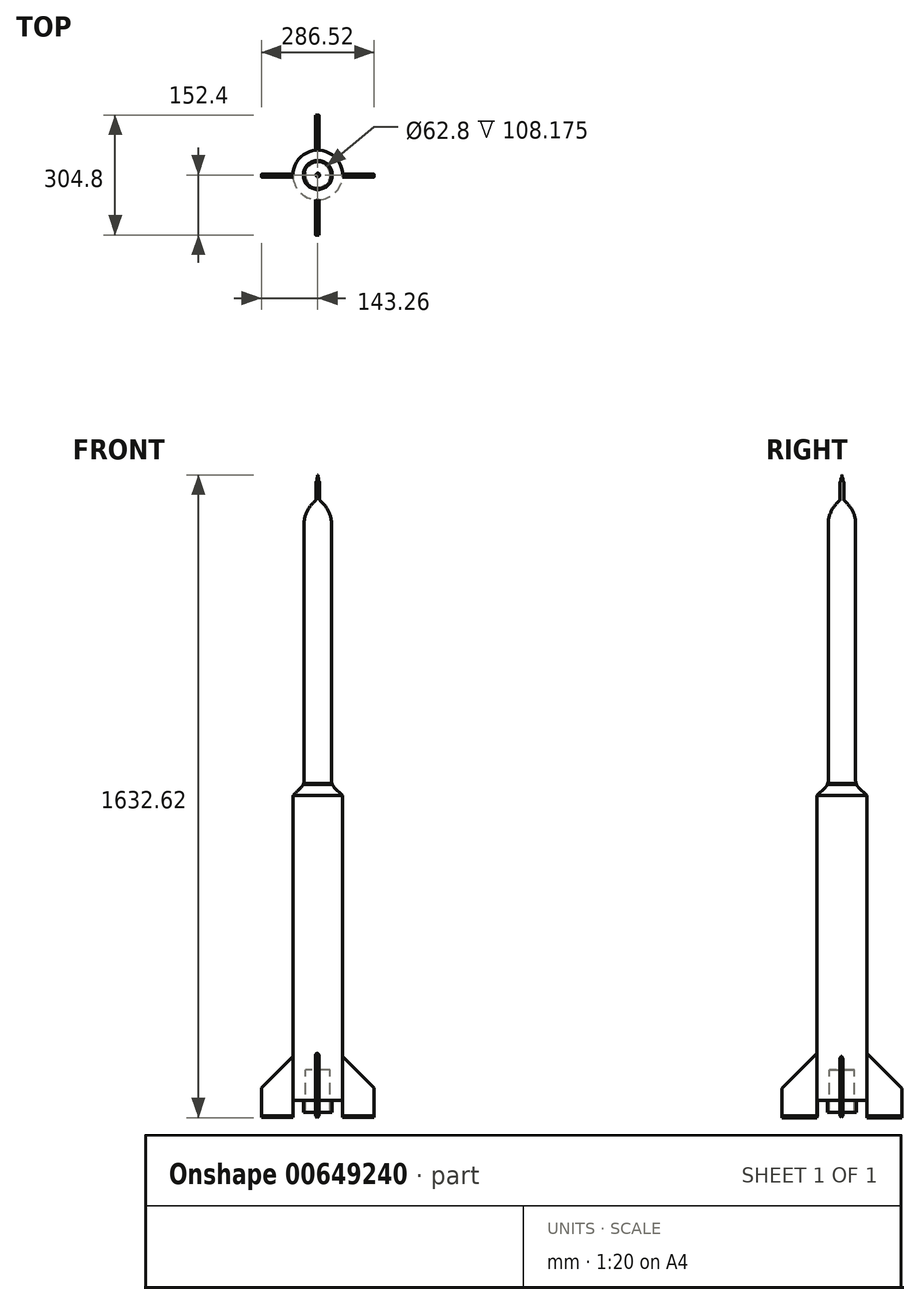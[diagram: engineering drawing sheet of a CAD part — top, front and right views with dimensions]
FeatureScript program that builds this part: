
annotation { "Feature Type Name" : "Feature", "Feature Type Description" : "" }
export const myFeature = defineFeature(function(context is Context, id is Id, definition is map)
    precondition{}
    {
        {
            var Q0;
            Q0=qCreatedBy(makeId("Top.planeOp"),FACE);
            var sketch = newSketch(context, id + "F0", { "sketchPlane" : qUnion([Q0])});
            skCircle(sketch, "E0", {"center": v(0, 0) * mm, "radius": 4.63 * mm});
            skSolve(sketch);
        }
        {
            var Q0;
            Q0 = qSketchRegion(id + "F0", true);
            extrude(context, id + "F1", {"entities" : qUnion([Q0]), "endBound" : BoundingType.SYMMETRIC, "depth" : 1539.24 * mm, "offsetDistance" : 25.4 * mm});
        }
        {
            var Q0;
            Q0=makeQuery(id+"F1.opExtrude","CAP_EDGE",EDGE,{"disambiguationData":[OSD([sQuery(id+"F0.wireOp",EDGE,"E0")])],"isStart":false});
            chamfer(context, id + "F2", {"entities" : qUnion([Q0]), "width" : 2.54 * mm, "tangentPropagation" : true});
        }
        {
            var Q0;
            Q0=qCreatedBy(makeId("Top.planeOp"),FACE);
            var sketch = newSketch(context, id + "F3", { "sketchPlane" : qUnion([Q0])});
            skCircle(sketch, "E1", {"center": v(0, 0) * mm, "radius": 2.08 * mm});
            skSolve(sketch);
        }
        {
            var Q0;
            Q0 = qSketchRegion(id + "F3", true);
            extrude(context, id + "F4", {"entities" : qUnion([Q0]), "operationType" : NewBodyOperationType.ADD, "depth" : 779.02 * mm, "offsetDistance" : 25.4 * mm});
        }
        {
            var Q0;
            Q0=makeQuery(id+"F4.opExtrude","CAP_EDGE",EDGE,{"disambiguationData":[OSD([sQuery(id+"F3.wireOp",EDGE,"E1")])],"isStart":false});
            chamfer(context, id + "F5", {"entities" : qUnion([Q0]), "width" : 2.03 * mm, "tangentPropagation" : true});
        }
        {
            var Q0;
            Q0=qCreatedBy(makeId("Top.planeOp"),FACE);
            var sketch = newSketch(context, id + "F6", { "sketchPlane" : qUnion([Q0])});
            skCircle(sketch, "E2", {"center": v(0, 0) * mm, "radius": 34.77 * mm});
            skSolve(sketch);
        }
        {
            var Q0;
            Q0 = qSketchRegion(id + "F6", true);
            extrude(context, id + "F7", {"entities" : qUnion([Q0]), "operationType" : NewBodyOperationType.ADD, "depth" : 720.85 * mm, "offsetDistance" : 25.4 * mm});
        }
        {
            var Q0;
            Q0=makeQuery(id+"F7.opExtrude","CAP_EDGE",EDGE,{"disambiguationData":[OSD([sQuery(id+"F6.wireOp",EDGE,"E2")])],"isStart":false});
            chamfer(context, id + "F8", {"entities" : qUnion([Q0]), "width" : 30.48 * mm, "tangentPropagation" : true});
        }
        {
            var Q0;
            Q0=qCreatedBy(makeId("Top.planeOp"),FACE);
            var sketch = newSketch(context, id + "F9", { "sketchPlane" : qUnion([Q0])});
            skCircle(sketch, "E3", {"center": v(0, 0) * mm, "radius": 63.15 * mm});
            skSolve(sketch);
        }
        {
            var Q0;
            Q0 = qSketchRegion(id + "F9", true);
            extrude(context, id + "F10", {"entities" : qUnion([Q0]), "operationType" : NewBodyOperationType.ADD, "oppositeDirection" : true, "depth" : 774.7 * mm, "offsetDistance" : 25.4 * mm});
        }
        {
            var Q0;
            Q0=makeQuery(id+"F10.opExtrude","CAP_EDGE",EDGE,{"disambiguationData":[OSD([sQuery(id+"F9.wireOp",EDGE,"E3")])],"isStart":true});
            chamfer(context, id + "F11", {"entities" : qUnion([Q0]), "width" : 30.48 * mm, "tangentPropagation" : true});
        }
        {
            var Q0;
            Q0=makeQuery(id+"F11.opChamfer","BLEND_EDGE",EDGE,{"blendedFrom":[makeQuery(id+"F10.opExtrude","CAP_EDGE",EDGE,{"disambiguationData":[OSD([sQuery(id+"F9.wireOp",EDGE,"E3")])],"isStart":true}),makeQuery(id+"F7.opExtrude","SWEPT_FACE",FACE,{"disambiguationData":[OSD([sQuery(id+"F6.wireOp",EDGE,"E2")])]})],"blendedInto":[makeQuery(id+"F7.opExtrude","SWEPT_FACE",FACE,{"disambiguationData":[OSD([sQuery(id+"F6.wireOp",EDGE,"E2")])]})]});
            fillet(context, id + "F12", {"entities" : qUnion([Q0]), "radius" : 24.66 * mm, "tangentPropagation" : true, "allowEdgeOverflow" : false});
        }
        {
            var Q0;
            {var subQ0=sQuery(id+"F0.wireOp",EDGE,"E0");var subQ1=sQuery(id+"F6.wireOp",EDGE,"E2");Q0=makeQuery(id+"F8.opChamfer","BLEND_EDGE",EDGE,{"blendedFrom":[makeQuery(id+"F7.opExtrude","CAP_EDGE",EDGE,{"disambiguationData":[OSD([subQ1])],"isStart":false}),makeQuery(id+"F7.boolean.opBoolean","SPLIT",FACE,{"disambiguationData":[TD([makeQuery(id+"F2.opChamfer","BLEND_FACE",FACE,{"disambiguationData":[OSD([subQ0])]})])],"derivedFrom":makeQuery(id+"F1.opExtrude","SWEPT_FACE",FACE,{"disambiguationData":[OSD([subQ0])]})})],"blendedInto":[makeQuery(id+"F7.boolean.opBoolean","SPLIT",FACE,{"disambiguationData":[TD([makeQuery(id+"F2.opChamfer","BLEND_FACE",FACE,{"disambiguationData":[OSD([subQ0])]})])],"derivedFrom":makeQuery(id+"F1.opExtrude","SWEPT_FACE",FACE,{"disambiguationData":[OSD([subQ0])]})})]});}
            fillet(context, id + "F13", {"entities" : qUnion([Q0]), "radius" : 5.08 * mm, "tangentPropagation" : true, "allowEdgeOverflow" : false});
        }
        {
            var Q0;
            {var subQ0=sQuery(id+"F0.wireOp",EDGE,"E0");Q0=makeQuery(id+"F2.opChamfer","BLEND_EDGE",EDGE,{"blendedFrom":[makeQuery(id+"F1.opExtrude","CAP_EDGE",EDGE,{"disambiguationData":[OSD([subQ0])],"isStart":false}),makeQuery(id+"F1.opExtrude","CAP_FACE",FACE,{"disambiguationData":[OSD([subQ0])],"isStart":false})],"blendedInto":[makeQuery(id+"F1.opExtrude","CAP_FACE",FACE,{"disambiguationData":[OSD([subQ0])],"isStart":false})]});}
            fillet(context, id + "F14", {"entities" : qUnion([Q0]), "radius" : 2.47 * mm, "tangentPropagation" : true, "allowEdgeOverflow" : false});
        }
        {
            var Q0;
            {var subQ0=sQuery(id+"F0.wireOp",EDGE,"E0");Q0=makeQuery(id+"F14.opFillet","BLEND_EDGE",EDGE,{"blendedFrom":[makeQuery(id+"F2.opChamfer","BLEND_EDGE",EDGE,{"blendedFrom":[makeQuery(id+"F1.opExtrude","CAP_EDGE",EDGE,{"disambiguationData":[OSD([subQ0])],"isStart":false}),makeQuery(id+"F1.opExtrude","CAP_FACE",FACE,{"disambiguationData":[OSD([subQ0])],"isStart":false})],"blendedInto":[makeQuery(id+"F1.opExtrude","CAP_FACE",FACE,{"disambiguationData":[OSD([subQ0])],"isStart":false})]}),makeQuery(id+"F4.opExtrude","SWEPT_FACE",FACE,{"disambiguationData":[OSD([sQuery(id+"F3.wireOp",EDGE,"E1")])]})],"blendedInto":[makeQuery(id+"F4.opExtrude","SWEPT_FACE",FACE,{"disambiguationData":[OSD([sQuery(id+"F3.wireOp",EDGE,"E1")])]})]});}
            fillet(context, id + "F15", {"entities" : qUnion([Q0]), "radius" : 2.64 * mm, "tangentPropagation" : true, "allowEdgeOverflow" : false});
        }
        {
            var Q0;
            Q0=qCreatedBy(makeId("Front.planeOp"),FACE);
            var sketch = newSketch(context, id + "F16", { "sketchPlane" : qUnion([Q0])});
            skLineSegment(sketch, "E4.bottom", {"start": v(-6.05, -685.08) * mm, "end": v(2.72, -685.08) * mm});
            skLineSegment(sketch, "E4.top", {"start": v(-6.05, -803.66) * mm, "end": v(2.72, -803.66) * mm});
            skLineSegment(sketch, "E4.left", {"start": v(-6.05, -685.08) * mm, "end": v(-6.05, -803.66) * mm});
            skLineSegment(sketch, "E4.right", {"start": v(2.72, -685.08) * mm, "end": v(2.72, -803.66) * mm});
            skSolve(sketch);
        }
        {
            var Q0;
            Q0 = qSketchRegion(id + "F16", true);
            extrude(context, id + "F17", {"entities" : qUnion([Q0]), "operationType" : NewBodyOperationType.ADD, "endBound" : BoundingType.SYMMETRIC, "depth" : 304.8 * mm, "offsetDistance" : 25.4 * mm});
        }
        {
            var Q0;
            Q0=makeQuery(id+"F17.opExtrude","CAP_EDGE",EDGE,{"disambiguationData":[OSD([sQuery(id+"F16.wireOp",EDGE,"E4.bottom")])],"isStart":false});
            var Q1;
            Q1=makeQuery(id+"F17.opExtrude","CAP_EDGE",EDGE,{"disambiguationData":[OSD([sQuery(id+"F16.wireOp",EDGE,"E4.bottom")])],"isStart":true});
            chamfer(context, id + "F18", {"entities" : qUnion([Q0, Q1]), "width" : 88.9 * mm, "tangentPropagation" : true});
        }
        {
            var Q0;
            Q0=qCreatedBy(makeId("Right.planeOp"),FACE);
            var sketch = newSketch(context, id + "F19", { "sketchPlane" : qUnion([Q0])});
            skLineSegment(sketch, "E5.bottom", {"start": v(2.04, -683.97) * mm, "end": v(-4.75, -683.97) * mm});
            skLineSegment(sketch, "E5.top", {"start": v(2.04, -803.67) * mm, "end": v(-4.75, -803.67) * mm});
            skLineSegment(sketch, "E5.left", {"start": v(2.04, -683.97) * mm, "end": v(2.04, -803.67) * mm});
            skLineSegment(sketch, "E5.right", {"start": v(-4.75, -683.97) * mm, "end": v(-4.75, -803.67) * mm});
            skSolve(sketch);
        }
        {
            var Q0;
            Q0 = qSketchRegion(id + "F19", true);
            extrude(context, id + "F20", {"entities" : qUnion([Q0]), "operationType" : NewBodyOperationType.ADD, "endBound" : BoundingType.SYMMETRIC, "oppositeDirection" : true, "depth" : 286.5 * mm, "offsetDistance" : 25.4 * mm});
        }
        {
            var Q0;
            Q0=makeQuery(id+"F20.opExtrude","CAP_EDGE",EDGE,{"disambiguationData":[OSD([sQuery(id+"F19.wireOp",EDGE,"E5.bottom")])],"isStart":false});
            var Q1;
            Q1=makeQuery(id+"F20.opExtrude","CAP_EDGE",EDGE,{"disambiguationData":[OSD([sQuery(id+"F19.wireOp",EDGE,"E5.bottom")])],"isStart":true});
            chamfer(context, id + "F21", {"entities" : qUnion([Q0, Q1]), "width" : 88.9 * mm, "tangentPropagation" : true});
        }
        {
            var Q0;
            Q0=qCreatedBy(makeId("Top.planeOp"),FACE);
            var sketch = newSketch(context, id + "F22", { "sketchPlane" : qUnion([Q0])});
            skCircle(sketch, "E6", {"center": v(0, 0) * mm, "radius": 63.15 * mm});
            skSolve(sketch);
        }
        {
            var Q0;
            Q0 = qSketchRegion(id + "F22", true);
            extrude(context, id + "F23", {"entities" : qUnion([Q0]), "operationType" : NewBodyOperationType.ADD, "oppositeDirection" : true, "depth" : 805.18 * mm, "offsetDistance" : 25.4 * mm});
        }
        {
            var Q0;
            {var subQ0=sQuery(id+"F19.wireOp",EDGE,"E5.right");var subQ1=sQuery(id+"F19.wireOp",EDGE,"E5.left");var subQ2=sQuery(id+"F19.wireOp",EDGE,"E5.top");Q0=makeQuery(id+"F23.boolean.opBoolean","SPLIT",FACE,{"disambiguationData":[TD([makeQuery(id+"F20.opExtrude","CAP_FACE",FACE,{"disambiguationData":[OSD([sQuery(id+"F19.wireOp",EDGE,"E5.bottom"),subQ2,subQ1,subQ0])],"isStart":true})])],"derivedFrom":makeQuery(id+"F20.opExtrude","SWEPT_FACE",FACE,{"disambiguationData":[OSD([subQ2])]})});}
            var Q1;
            {var subQ2=sQuery(id+"F16.wireOp",EDGE,"E4.top");Q1=makeQuery(id+"F20.boolean.opBoolean","SPLIT",FACE,{"disambiguationData":[TD([makeQuery(id+"F20.opExtrude","SWEPT_FACE",FACE,{"disambiguationData":[OSD([sQuery(id+"F19.wireOp",EDGE,"E5.right")])]})])],"derivedFrom":makeQuery(id+"F17.opExtrude","SWEPT_FACE",FACE,{"disambiguationData":[OSD([subQ2])]})});}
            var Q2;
            {var subQ2=sQuery(id+"F16.wireOp",EDGE,"E4.top");Q2=makeQuery(id+"F20.boolean.opBoolean","SPLIT",FACE,{"disambiguationData":[TD([makeQuery(id+"F20.opExtrude","SWEPT_FACE",FACE,{"disambiguationData":[OSD([sQuery(id+"F19.wireOp",EDGE,"E5.left")])]})])],"derivedFrom":makeQuery(id+"F17.opExtrude","SWEPT_FACE",FACE,{"disambiguationData":[OSD([subQ2])]})});}
            var Q3;
            {var subQ0=sQuery(id+"F19.wireOp",EDGE,"E5.right");var subQ1=sQuery(id+"F19.wireOp",EDGE,"E5.left");var subQ2=sQuery(id+"F19.wireOp",EDGE,"E5.top");Q3=makeQuery(id+"F23.boolean.opBoolean","SPLIT",FACE,{"disambiguationData":[TD([makeQuery(id+"F20.opExtrude","CAP_FACE",FACE,{"disambiguationData":[OSD([sQuery(id+"F19.wireOp",EDGE,"E5.bottom"),subQ2,subQ1,subQ0])],"isStart":false})])],"derivedFrom":makeQuery(id+"F20.opExtrude","SWEPT_FACE",FACE,{"disambiguationData":[OSD([subQ2])]})});}
            extrude(context, id + "F24", {"entities" : qUnion([Q0, Q1, Q2, Q3]), "operationType" : NewBodyOperationType.ADD, "depth" : 45.72 * mm, "offsetDistance" : 25.4 * mm});
        }
        {
            var Q0;
            Q0=makeQuery(id+"F23.opExtrude","CAP_EDGE",EDGE,{"disambiguationData":[OSD([sQuery(id+"F22.wireOp",EDGE,"E6")])],"isStart":true});
            chamfer(context, id + "F25", {"entities" : qUnion([Q0]), "width" : 30.48 * mm, "tangentPropagation" : true});
        }
        {
            var Q0;
            Q0=makeQuery(id+"F21.opChamfer","BLEND_EDGE",EDGE,{"blendedFrom":[makeQuery(id+"F20.opExtrude","CAP_EDGE",EDGE,{"disambiguationData":[OSD([sQuery(id+"F19.wireOp",EDGE,"E5.bottom")])],"isStart":true}),makeQuery(id+"F20.opExtrude","SWEPT_FACE",FACE,{"disambiguationData":[OSD([sQuery(id+"F19.wireOp",EDGE,"E5.left")])]})],"blendedInto":[makeQuery(id+"F20.opExtrude","SWEPT_FACE",FACE,{"disambiguationData":[OSD([sQuery(id+"F19.wireOp",EDGE,"E5.left")])]})]});
            var Q1;
            Q1=makeQuery(id+"F21.opChamfer","BLEND_EDGE",EDGE,{"blendedFrom":[makeQuery(id+"F20.opExtrude","CAP_EDGE",EDGE,{"disambiguationData":[OSD([sQuery(id+"F19.wireOp",EDGE,"E5.bottom")])],"isStart":true}),makeQuery(id+"F20.opExtrude","SWEPT_FACE",FACE,{"disambiguationData":[OSD([sQuery(id+"F19.wireOp",EDGE,"E5.right")])]})],"blendedInto":[makeQuery(id+"F20.opExtrude","SWEPT_FACE",FACE,{"disambiguationData":[OSD([sQuery(id+"F19.wireOp",EDGE,"E5.right")])]})]});
            var Q2;
            Q2=makeQuery(id+"F18.opChamfer","BLEND_EDGE",EDGE,{"blendedFrom":[makeQuery(id+"F17.opExtrude","CAP_EDGE",EDGE,{"disambiguationData":[OSD([sQuery(id+"F16.wireOp",EDGE,"E4.bottom")])],"isStart":true}),makeQuery(id+"F17.opExtrude","SWEPT_FACE",FACE,{"disambiguationData":[OSD([sQuery(id+"F16.wireOp",EDGE,"E4.right")])]})],"blendedInto":[makeQuery(id+"F17.opExtrude","SWEPT_FACE",FACE,{"disambiguationData":[OSD([sQuery(id+"F16.wireOp",EDGE,"E4.right")])]})]});
            var Q3;
            Q3=makeQuery(id+"F18.opChamfer","BLEND_EDGE",EDGE,{"blendedFrom":[makeQuery(id+"F17.opExtrude","CAP_EDGE",EDGE,{"disambiguationData":[OSD([sQuery(id+"F16.wireOp",EDGE,"E4.bottom")])],"isStart":true}),makeQuery(id+"F17.opExtrude","SWEPT_FACE",FACE,{"disambiguationData":[OSD([sQuery(id+"F16.wireOp",EDGE,"E4.left")])]})],"blendedInto":[makeQuery(id+"F17.opExtrude","SWEPT_FACE",FACE,{"disambiguationData":[OSD([sQuery(id+"F16.wireOp",EDGE,"E4.left")])]})]});
            var Q4;
            Q4=makeQuery(id+"F21.opChamfer","BLEND_EDGE",EDGE,{"blendedFrom":[makeQuery(id+"F20.opExtrude","CAP_EDGE",EDGE,{"disambiguationData":[OSD([sQuery(id+"F19.wireOp",EDGE,"E5.bottom")])],"isStart":false}),makeQuery(id+"F20.opExtrude","SWEPT_FACE",FACE,{"disambiguationData":[OSD([sQuery(id+"F19.wireOp",EDGE,"E5.left")])]})],"blendedInto":[makeQuery(id+"F20.opExtrude","SWEPT_FACE",FACE,{"disambiguationData":[OSD([sQuery(id+"F19.wireOp",EDGE,"E5.left")])]})]});
            var Q5;
            Q5=makeQuery(id+"F21.opChamfer","BLEND_EDGE",EDGE,{"blendedFrom":[makeQuery(id+"F20.opExtrude","CAP_EDGE",EDGE,{"disambiguationData":[OSD([sQuery(id+"F19.wireOp",EDGE,"E5.bottom")])],"isStart":false}),makeQuery(id+"F20.opExtrude","SWEPT_FACE",FACE,{"disambiguationData":[OSD([sQuery(id+"F19.wireOp",EDGE,"E5.right")])]})],"blendedInto":[makeQuery(id+"F20.opExtrude","SWEPT_FACE",FACE,{"disambiguationData":[OSD([sQuery(id+"F19.wireOp",EDGE,"E5.right")])]})]});
            var Q6;
            Q6=makeQuery(id+"F18.opChamfer","BLEND_EDGE",EDGE,{"blendedFrom":[makeQuery(id+"F17.opExtrude","CAP_EDGE",EDGE,{"disambiguationData":[OSD([sQuery(id+"F16.wireOp",EDGE,"E4.bottom")])],"isStart":false}),makeQuery(id+"F17.opExtrude","SWEPT_FACE",FACE,{"disambiguationData":[OSD([sQuery(id+"F16.wireOp",EDGE,"E4.right")])]})],"blendedInto":[makeQuery(id+"F17.opExtrude","SWEPT_FACE",FACE,{"disambiguationData":[OSD([sQuery(id+"F16.wireOp",EDGE,"E4.right")])]})]});
            var Q7;
            Q7=makeQuery(id+"F18.opChamfer","BLEND_EDGE",EDGE,{"blendedFrom":[makeQuery(id+"F17.opExtrude","CAP_EDGE",EDGE,{"disambiguationData":[OSD([sQuery(id+"F16.wireOp",EDGE,"E4.bottom")])],"isStart":false}),makeQuery(id+"F17.opExtrude","SWEPT_FACE",FACE,{"disambiguationData":[OSD([sQuery(id+"F16.wireOp",EDGE,"E4.left")])]})],"blendedInto":[makeQuery(id+"F17.opExtrude","SWEPT_FACE",FACE,{"disambiguationData":[OSD([sQuery(id+"F16.wireOp",EDGE,"E4.left")])]})]});
            fillet(context, id + "F26", {"entities" : qUnion([Q0, Q1, Q2, Q3, Q4, Q5, Q6, Q7]), "radius" : 5.08 * mm, "tangentPropagation" : true, "allowEdgeOverflow" : false});
        }
        {
            var Q0;
            {var subQ0=sQuery(id+"F16.wireOp",EDGE,"E4.left");var subQ1=sQuery(id+"F16.wireOp",EDGE,"E4.top");Q0=makeQuery(id+"F24.opExtrude","CAP_EDGE",EDGE,{"disambiguationData":[OSD([subQ1,subQ0]),TDD([makeQuery(id+"F20.boolean.opBoolean","SPLIT",EDGE,{"disambiguationData":[TD([makeQuery(id+"F20.opExtrude","SWEPT_FACE",FACE,{"disambiguationData":[OSD([sQuery(id+"F19.wireOp",EDGE,"E5.right")])]})])],"derivedFrom":makeQuery(id+"F17.opExtrude","SWEPT_EDGE",EDGE,{"disambiguationData":[OSD([subQ1,subQ0])]})})])],"isStart":false});}
            var Q1;
            {var subQ0=sQuery(id+"F16.wireOp",EDGE,"E4.right");var subQ1=sQuery(id+"F16.wireOp",EDGE,"E4.top");Q1=makeQuery(id+"F24.opExtrude","CAP_EDGE",EDGE,{"disambiguationData":[OSD([subQ1,subQ0]),TDD([makeQuery(id+"F20.boolean.opBoolean","SPLIT",EDGE,{"disambiguationData":[TD([makeQuery(id+"F20.opExtrude","SWEPT_FACE",FACE,{"disambiguationData":[OSD([sQuery(id+"F19.wireOp",EDGE,"E5.right")])]})])],"derivedFrom":makeQuery(id+"F17.opExtrude","SWEPT_EDGE",EDGE,{"disambiguationData":[OSD([subQ1,subQ0])]})})])],"isStart":false});}
            var Q2;
            {var subQ0=sQuery(id+"F19.wireOp",EDGE,"E5.left");var subQ1=sQuery(id+"F19.wireOp",EDGE,"E5.top");Q2=makeQuery(id+"F24.opExtrude","CAP_EDGE",EDGE,{"disambiguationData":[OSD([subQ1,subQ0]),TDD([makeQuery(id+"F23.boolean.opBoolean","SPLIT",EDGE,{"disambiguationData":[TD([makeQuery(id+"F20.opExtrude","CAP_FACE",FACE,{"disambiguationData":[OSD([sQuery(id+"F19.wireOp",EDGE,"E5.bottom"),subQ1,subQ0,sQuery(id+"F19.wireOp",EDGE,"E5.right")])],"isStart":false})])],"derivedFrom":makeQuery(id+"F20.opExtrude","SWEPT_EDGE",EDGE,{"disambiguationData":[OSD([subQ1,subQ0])]})})])],"isStart":false});}
            var Q3;
            {var subQ0=sQuery(id+"F19.wireOp",EDGE,"E5.right");var subQ1=sQuery(id+"F19.wireOp",EDGE,"E5.top");Q3=makeQuery(id+"F24.opExtrude","CAP_EDGE",EDGE,{"disambiguationData":[OSD([subQ1,subQ0]),TDD([makeQuery(id+"F23.boolean.opBoolean","SPLIT",EDGE,{"disambiguationData":[TD([makeQuery(id+"F20.opExtrude","CAP_FACE",FACE,{"disambiguationData":[OSD([sQuery(id+"F19.wireOp",EDGE,"E5.bottom"),subQ1,sQuery(id+"F19.wireOp",EDGE,"E5.left"),subQ0])],"isStart":false})])],"derivedFrom":makeQuery(id+"F20.opExtrude","SWEPT_EDGE",EDGE,{"disambiguationData":[OSD([subQ1,subQ0])]})})])],"isStart":false});}
            var Q4;
            {var subQ0=sQuery(id+"F16.wireOp",EDGE,"E4.left");var subQ1=sQuery(id+"F16.wireOp",EDGE,"E4.top");Q4=makeQuery(id+"F24.opExtrude","CAP_EDGE",EDGE,{"disambiguationData":[OSD([subQ1,subQ0]),TDD([makeQuery(id+"F20.boolean.opBoolean","SPLIT",EDGE,{"disambiguationData":[TD([makeQuery(id+"F20.opExtrude","SWEPT_FACE",FACE,{"disambiguationData":[OSD([sQuery(id+"F19.wireOp",EDGE,"E5.left")])]})])],"derivedFrom":makeQuery(id+"F17.opExtrude","SWEPT_EDGE",EDGE,{"disambiguationData":[OSD([subQ1,subQ0])]})})])],"isStart":false});}
            var Q5;
            {var subQ0=sQuery(id+"F16.wireOp",EDGE,"E4.right");var subQ1=sQuery(id+"F16.wireOp",EDGE,"E4.top");Q5=makeQuery(id+"F24.opExtrude","CAP_EDGE",EDGE,{"disambiguationData":[OSD([subQ1,subQ0]),TDD([makeQuery(id+"F20.boolean.opBoolean","SPLIT",EDGE,{"disambiguationData":[TD([makeQuery(id+"F20.opExtrude","SWEPT_FACE",FACE,{"disambiguationData":[OSD([sQuery(id+"F19.wireOp",EDGE,"E5.left")])]})])],"derivedFrom":makeQuery(id+"F17.opExtrude","SWEPT_EDGE",EDGE,{"disambiguationData":[OSD([subQ1,subQ0])]})})])],"isStart":false});}
            var Q6;
            {var subQ0=sQuery(id+"F19.wireOp",EDGE,"E5.right");var subQ1=sQuery(id+"F19.wireOp",EDGE,"E5.top");Q6=makeQuery(id+"F24.opExtrude","CAP_EDGE",EDGE,{"disambiguationData":[OSD([subQ1,subQ0]),TDD([makeQuery(id+"F23.boolean.opBoolean","SPLIT",EDGE,{"disambiguationData":[TD([makeQuery(id+"F20.opExtrude","CAP_FACE",FACE,{"disambiguationData":[OSD([sQuery(id+"F19.wireOp",EDGE,"E5.bottom"),subQ1,sQuery(id+"F19.wireOp",EDGE,"E5.left"),subQ0])],"isStart":true})])],"derivedFrom":makeQuery(id+"F20.opExtrude","SWEPT_EDGE",EDGE,{"disambiguationData":[OSD([subQ1,subQ0])]})})])],"isStart":false});}
            var Q7;
            {var subQ0=sQuery(id+"F19.wireOp",EDGE,"E5.left");var subQ1=sQuery(id+"F19.wireOp",EDGE,"E5.top");Q7=makeQuery(id+"F24.opExtrude","CAP_EDGE",EDGE,{"disambiguationData":[OSD([subQ1,subQ0]),TDD([makeQuery(id+"F23.boolean.opBoolean","SPLIT",EDGE,{"disambiguationData":[TD([makeQuery(id+"F20.opExtrude","CAP_FACE",FACE,{"disambiguationData":[OSD([sQuery(id+"F19.wireOp",EDGE,"E5.bottom"),subQ1,subQ0,sQuery(id+"F19.wireOp",EDGE,"E5.right")])],"isStart":true})])],"derivedFrom":makeQuery(id+"F20.opExtrude","SWEPT_EDGE",EDGE,{"disambiguationData":[OSD([subQ1,subQ0])]})})])],"isStart":false});}
            chamfer(context, id + "F27", {"entities" : qUnion([Q0, Q1, Q2, Q3, Q4, Q5, Q6, Q7]), "width" : 5.08 * mm, "tangentPropagation" : true});
        }
        {
            var Q0;
            Q0=qCreatedBy(makeId("Top.planeOp"),FACE);
            var sketch = newSketch(context, id + "F28", { "sketchPlane" : qUnion([Q0])});
            skCircle(sketch, "E7", {"center": v(0, 0) * mm, "radius": 18.48 * mm});
            skSolve(sketch);
        }
        {
            var Q0;
            Q0 = qSketchRegion(id + "F28", true);
            extrude(context, id + "F29", {"entities" : qUnion([Q0]), "operationType" : NewBodyOperationType.ADD, "oppositeDirection" : true, "depth" : 820.42 * mm, "offsetDistance" : 25.4 * mm});
        }
        {
            var Q0;
            Q0=qCreatedBy(makeId("Top.planeOp"),FACE);
            var sketch = newSketch(context, id + "F30", { "sketchPlane" : qUnion([Q0])});
            skCircle(sketch, "E8", {"center": v(0, 0) * mm, "radius": 36.77 * mm});
            skSolve(sketch);
        }
        {
            var Q0;
            Q0 = qSketchRegion(id + "F30", true);
            extrude(context, id + "F31", {"entities" : qUnion([Q0]), "operationType" : NewBodyOperationType.ADD, "oppositeDirection" : true, "depth" : 835.66 * mm, "offsetDistance" : 25.4 * mm});
        }
        {
            var Q0;
            Q0=qCreatedBy(makeId("Top.planeOp"),FACE);
            var sketch = newSketch(context, id + "F32", { "sketchPlane" : qUnion([Q0])});
            skCircle(sketch, "E9", {"center": v(0, 0) * mm, "radius": 31.4 * mm});
            skSolve(sketch);
        }
        {
            var Q0;
            Q0 = qSketchRegion(id + "F32", true);
            extrude(context, id + "F33", {"entities" : qUnion([Q0]), "operationType" : NewBodyOperationType.REMOVE, "oppositeDirection" : true, "depth" : 1024.93 * mm, "offsetDistance" : 25.4 * mm});
        }
        {
            var Q0;
            Q0=qCreatedBy(makeId("Top.planeOp"),FACE);
            var sketch = newSketch(context, id + "F34", { "sketchPlane" : qUnion([Q0])});
            skCircle(sketch, "E10", {"center": v(0, 0) * mm, "radius": 31.4 * mm});
            skSolve(sketch);
        }
        {
            var Q0;
            Q0 = qSketchRegion(id + "F34", true);
            extrude(context, id + "F35", {"entities" : qUnion([Q0]), "operationType" : NewBodyOperationType.ADD, "oppositeDirection" : true, "depth" : 727.5 * mm, "offsetDistance" : 25.4 * mm});
        }
        {
            var Q0;
            {var subQ0=sQuery(id+"F6.wireOp",EDGE,"E2");Q0=makeQuery(id+"F8.opChamfer","BLEND_EDGE",EDGE,{"blendedFrom":[makeQuery(id+"F7.opExtrude","CAP_EDGE",EDGE,{"disambiguationData":[OSD([subQ0])],"isStart":false}),makeQuery(id+"F7.opExtrude","SWEPT_FACE",FACE,{"disambiguationData":[OSD([subQ0])]})],"blendedInto":[makeQuery(id+"F7.opExtrude","SWEPT_FACE",FACE,{"disambiguationData":[OSD([subQ0])]})]});}
            fillet(context, id + "F36", {"entities" : qUnion([Q0]), "radius" : 75.64 * mm, "tangentPropagation" : true, "allowEdgeOverflow" : false});
        }
        {
            var Q0;
            {var subQ0=sQuery(id+"F0.wireOp",EDGE,"E0");Q0=makeQuery(id+"F2.opChamfer","BLEND_EDGE",EDGE,{"blendedFrom":[makeQuery(id+"F1.opExtrude","CAP_EDGE",EDGE,{"disambiguationData":[OSD([subQ0])],"isStart":false}),makeQuery(id+"F1.opExtrude","SWEPT_FACE",FACE,{"disambiguationData":[OSD([subQ0])]})],"blendedInto":[makeQuery(id+"F1.opExtrude","SWEPT_FACE",FACE,{"disambiguationData":[OSD([subQ0])]})]});}
            fillet(context, id + "F37", {"entities" : qUnion([Q0]), "radius" : 5.08 * mm, "tangentPropagation" : true, "allowEdgeOverflow" : false});
        }
        {
            var Q0;
            {var subQ0=sQuery(id+"F3.wireOp",EDGE,"E1");Q0=makeQuery(id+"F5.opChamfer","BLEND_EDGE",EDGE,{"blendedFrom":[makeQuery(id+"F4.opExtrude","CAP_EDGE",EDGE,{"disambiguationData":[OSD([subQ0])],"isStart":false}),makeQuery(id+"F4.opExtrude","SWEPT_FACE",FACE,{"disambiguationData":[OSD([subQ0])]})],"blendedInto":[makeQuery(id+"F4.opExtrude","SWEPT_FACE",FACE,{"disambiguationData":[OSD([subQ0])]})]});}
            fillet(context, id + "F38", {"entities" : qUnion([Q0]), "radius" : 5.08 * mm, "tangentPropagation" : true, "allowEdgeOverflow" : false});
        }
        {
            var Q0;
            Q0=makeQuery(id+"F4.opExtrude","CAP_FACE",FACE,{"disambiguationData":[OSD([sQuery(id+"F3.wireOp",EDGE,"E1")])],"isStart":false});
            extrude(context, id + "F39", {"entities" : qUnion([Q0]), "operationType" : NewBodyOperationType.ADD, "depth" : 4.9 * mm, "offsetDistance" : 25.4 * mm});
        }
    });
